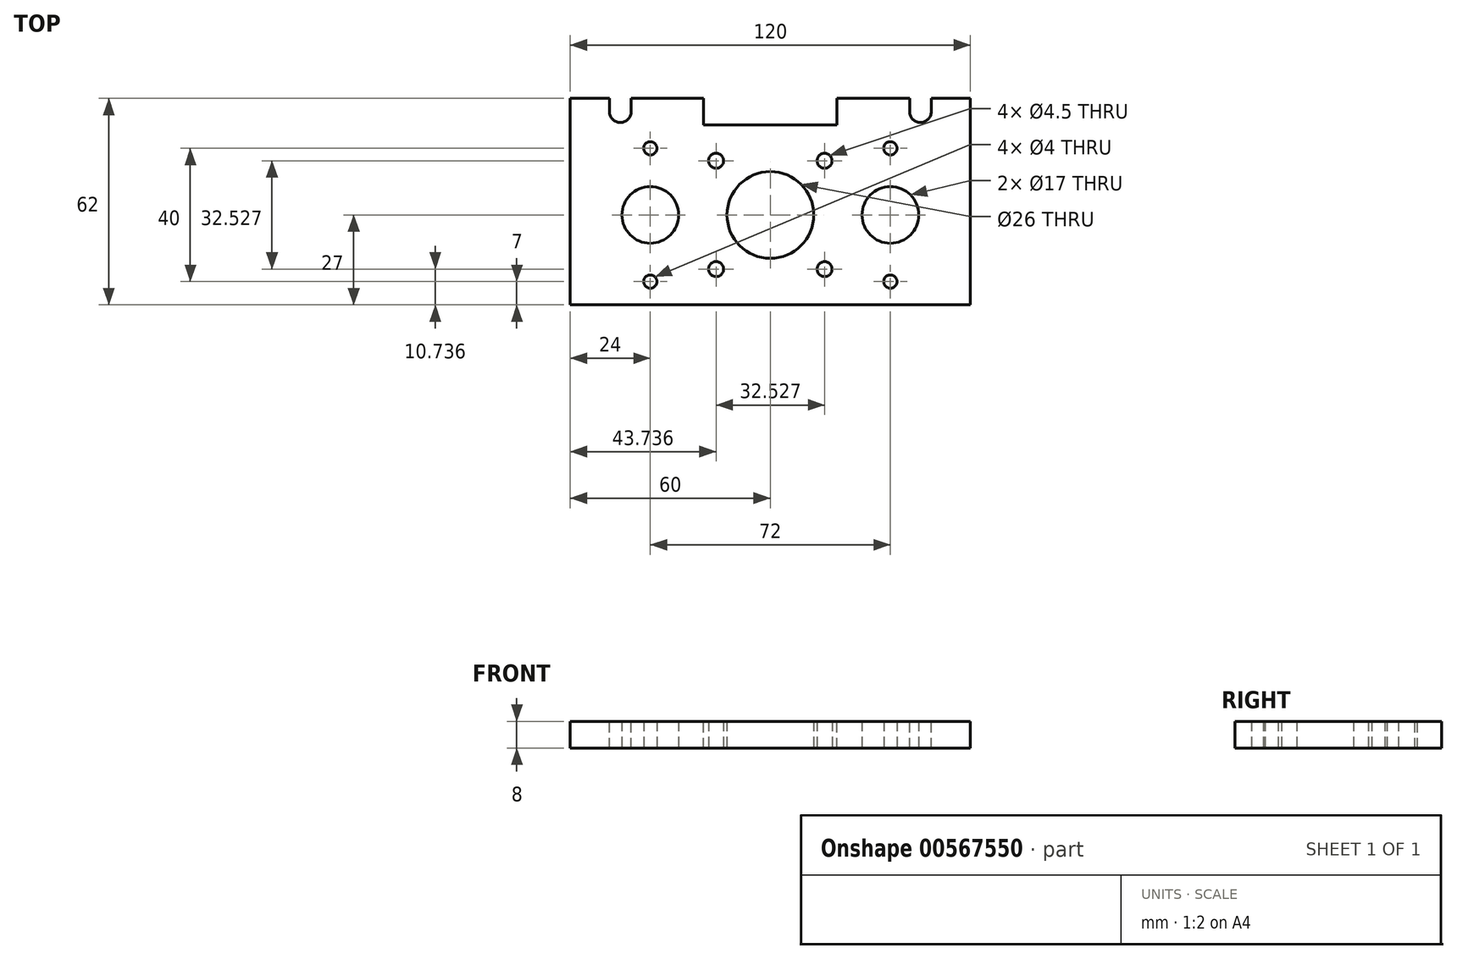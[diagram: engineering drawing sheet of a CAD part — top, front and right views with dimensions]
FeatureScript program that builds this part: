
annotation { "Feature Type Name" : "Feature", "Feature Type Description" : "" }
export const myFeature = defineFeature(function(context is Context, id is Id, definition is map)
    precondition{}
    {
        {
            var Q0;
            Q0=qCreatedBy(makeId("Top.planeOp"),FACE);
            var sketch = newSketch(context, id + "F0", { "sketchPlane" : qUnion([Q0])});
            skLineSegment(sketch, "E0.bottom", {"start": v(60, -31) * mm, "end": v(-60, -31) * mm});
            skLineSegment(sketch, "E0.top", {"start": v(60, 31) * mm, "end": v(-60, 31) * mm});
            skLineSegment(sketch, "E0.left", {"start": v(60, -31) * mm, "end": v(60, 31) * mm});
            skLineSegment(sketch, "E0.right", {"start": v(-60, -31) * mm, "end": v(-60, 31) * mm});
            skPoint(sketch, "E0.middle", {"position": v(0, 0) * mm});
            skCircle(sketch, "E1", {"center": v(-36, -4) * mm, "radius": 8.5 * mm});
            skCircle(sketch, "E2", {"center": v(36, -4) * mm, "radius": 8.5 * mm});
            skLineSegment(sketch, "E3", {"start": v(-36, -4) * mm, "end": v(36, -4) * mm, "construction": true});
            skCircle(sketch, "E4", {"center": v(0, -4) * mm, "radius": 23 * mm, "construction": true});
            skLineSegment(sketch, "E5.bottom", {"start": v(16.26, -20.26) * mm, "end": v(-16.26, -20.26) * mm, "construction": true});
            skLineSegment(sketch, "E5.top", {"start": v(16.26, 12.26) * mm, "end": v(-16.26, 12.26) * mm, "construction": true});
            skLineSegment(sketch, "E5.left", {"start": v(16.26, -20.26) * mm, "end": v(16.26, 12.26) * mm, "construction": true});
            skLineSegment(sketch, "E5.right", {"start": v(-16.26, -20.26) * mm, "end": v(-16.26, 12.26) * mm, "construction": true});
            skCircle(sketch, "E6", {"center": v(-16.26, 12.26) * mm, "radius": 2.25 * mm});
            skCircle(sketch, "E7", {"center": v(16.26, 12.26) * mm, "radius": 2.25 * mm});
            skCircle(sketch, "E8", {"center": v(16.26, -20.26) * mm, "radius": 2.25 * mm});
            skCircle(sketch, "E9", {"center": v(-16.26, -20.26) * mm, "radius": 2.25 * mm});
            skCircle(sketch, "E10", {"center": v(0, -4) * mm, "radius": 13 * mm});
            skCircle(sketch, "E11", {"center": v(-36, -24) * mm, "radius": 2 * mm});
            skCircle(sketch, "E12", {"center": v(-36, 16) * mm, "radius": 2 * mm});
            skCircle(sketch, "E13", {"center": v(36, 16) * mm, "radius": 2 * mm});
            skCircle(sketch, "E14", {"center": v(36, -24) * mm, "radius": 2 * mm});
            skSolve(sketch);
        }
        {
            var Q0;
            Q0 = qSketchRegion(id + "F0", true);
            extrude(context, id + "F1", {"entities" : qUnion([Q0]), "depth" : 8 * mm, "offsetDistance" : 25 * mm});
        }
        {
            var Q0;
            Q0=makeQuery(id+"F1.opExtrude","CAP_FACE",FACE,{"disambiguationData":[OSD([sQuery(id+"F0.wireOp",EDGE,"E0.bottom"),sQuery(id+"F0.wireOp",EDGE,"E0.top"),sQuery(id+"F0.wireOp",EDGE,"E0.left"),sQuery(id+"F0.wireOp",EDGE,"E0.right"),sQuery(id+"F0.wireOp",EDGE,"E1"),sQuery(id+"F0.wireOp",EDGE,"E2")])],"isStart":false});
            var sketch = newSketch(context, id + "F2", { "sketchPlane" : qUnion([Q0])});
            skLineSegment(sketch, "E15.bottom", {"start": v(-20, 31) * mm, "end": v(20, 31) * mm});
            skLineSegment(sketch, "E15.top", {"start": v(-20, 23) * mm, "end": v(20, 23) * mm});
            skLineSegment(sketch, "E15.left", {"start": v(-20, 31) * mm, "end": v(-20, 23) * mm});
            skLineSegment(sketch, "E15.right", {"start": v(20, 31) * mm, "end": v(20, 23) * mm});
            skArc(sketch, "E16", {"start": v(-48.25, 27) * mm, "mid": v(-45, 23.75) * mm, "end": v(-41.75, 27) * mm});
            skLineSegment(sketch, "E17", {"start": v(-41.75, 27) * mm, "end": v(-41.75, 31) * mm});
            skLineSegment(sketch, "E18", {"start": v(-48.25, 27) * mm, "end": v(-48.25, 31) * mm});
            skLineSegment(sketch, "E19", {"start": v(-48.25, 31) * mm, "end": v(-41.75, 31) * mm});
            skLineSegment(sketch, "E20.MirrorCS", {"start": v(41.75, 27) * mm, "end": v(41.75, 31) * mm});
            skArc(sketch, "E21.MirrorCS", {"start": v(48.25, 27) * mm, "mid": v(45, 23.75) * mm, "end": v(41.75, 27) * mm});
            skLineSegment(sketch, "E22.MirrorCS", {"start": v(48.25, 27) * mm, "end": v(48.25, 31) * mm});
            skLineSegment(sketch, "E23.MirrorCS", {"start": v(48.25, 31) * mm, "end": v(41.75, 31) * mm});
            skSolve(sketch);
        }
        {
            var Q0;
            Q0 = qSketchRegion(id + "F2", true);
            extrude(context, id + "F3", {"entities" : qUnion([Q0]), "operationType" : NewBodyOperationType.REMOVE, "endBound" : BoundingType.THROUGH_ALL, "oppositeDirection" : true, "depth" : 25 * mm, "offsetDistance" : 25 * mm});
        }
    });
